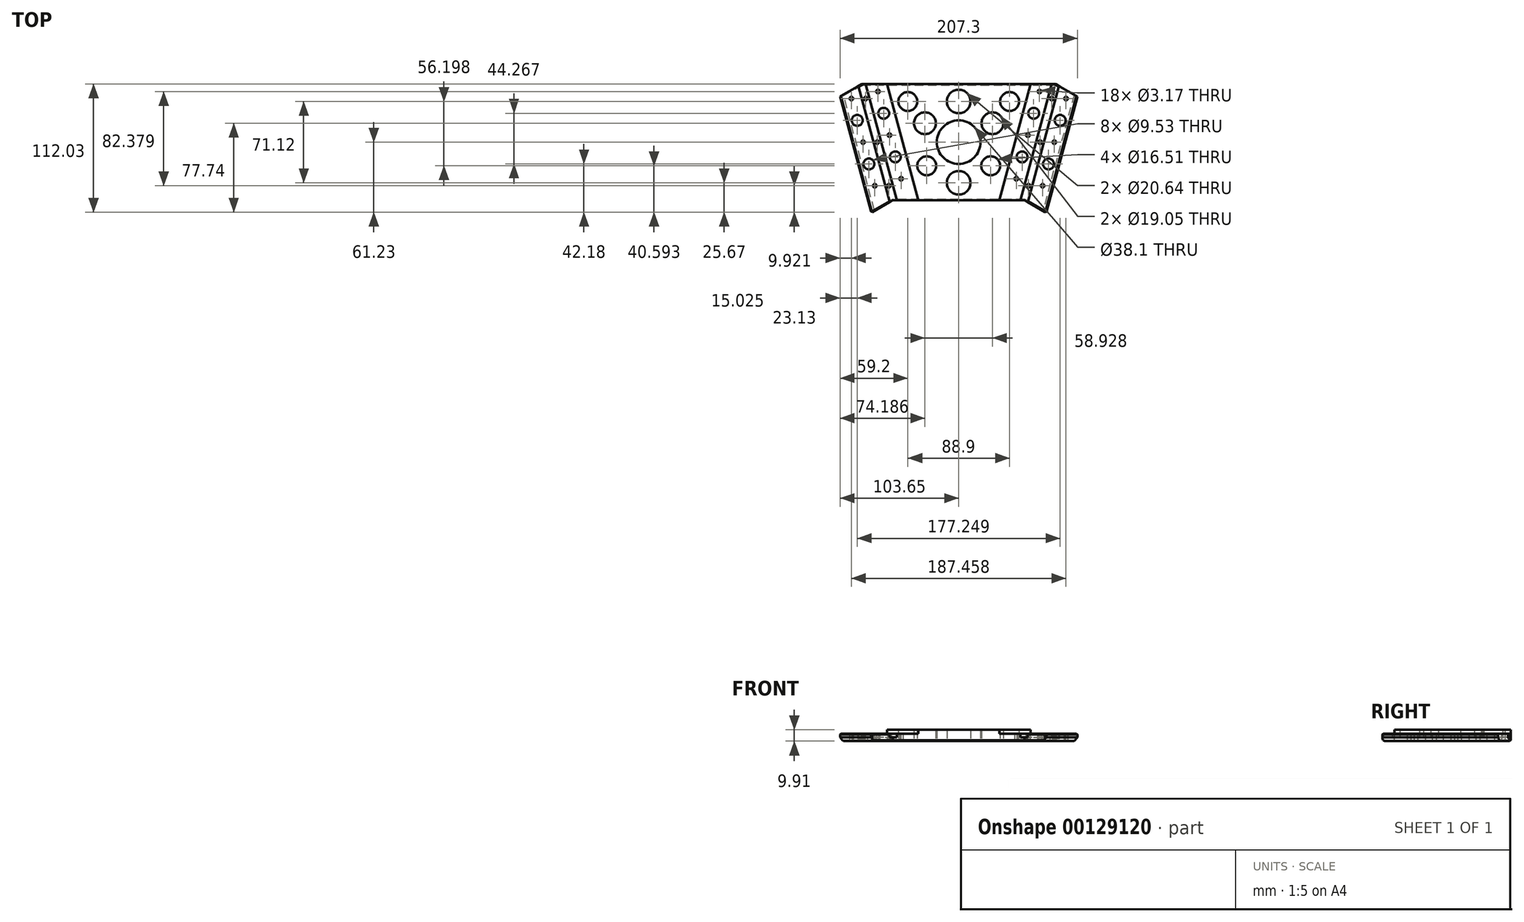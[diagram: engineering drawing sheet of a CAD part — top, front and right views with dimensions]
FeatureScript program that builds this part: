
annotation { "Feature Type Name" : "Feature", "Feature Type Description" : "" }
export const myFeature = defineFeature(function(context is Context, id is Id, definition is map)
    precondition{}
    {
        {
            var Q0;
            Q0=qCreatedBy(makeId("Top.planeOp"),FACE);
            var sketch = newSketch(context, id + "F0", { "sketchPlane" : qUnion([Q0])});
            skLineSegment(sketch, "E0", {"start": v(-79.38, -50.8) * mm, "end": v(0, -50.8) * mm});
            skLineSegment(sketch, "E1", {"start": v(0, -50.8) * mm, "end": v(0, 50.8) * mm});
            skLineSegment(sketch, "E2", {"start": v(0, 50.8) * mm, "end": v(-106.6, 50.8) * mm});
            skLineSegment(sketch, "E3", {"start": v(-106.6, 50.8) * mm, "end": v(-79.38, -50.8) * mm});
            skLineSegment(sketch, "E4.MirrorCS", {"start": v(0, 50.8) * mm, "end": v(106.6, 50.8) * mm});
            skLineSegment(sketch, "E5.MirrorCS", {"start": v(106.6, 50.8) * mm, "end": v(79.38, -50.8) * mm});
            skLineSegment(sketch, "E6.MirrorCS", {"start": v(79.38, -50.8) * mm, "end": v(0, -50.8) * mm});
            skSolve(sketch);
        }
        {
            var Q0;
            Q0=qSketchRegion(id+"F0",true);
            var Q1;
            Q1=qSketchRegion(id+"F2",true);
            extrude(context, id + "F1", {"entities" : qUnion([Q0, Q1]), "depth" : 13.08 * mm});
        }
        {
            var Q0;
            Q0=makeQuery(id+"F1.opExtrude","CAP_FACE",FACE,{"disambiguationData":[OSD([sQuery(id+"F0.wireOp",EDGE,"E0"),sQuery(id+"F0.wireOp",EDGE,"E1"),sQuery(id+"F0.wireOp",EDGE,"E2"),sQuery(id+"F0.wireOp",EDGE,"E3")])],"isStart":false});
            var sketch = newSketch(context, id + "F2", { "sketchPlane" : qUnion([Q0])});
            skLineSegment(sketch, "E7", {"start": v(-87.93, 50.8) * mm, "end": v(-60.7, -50.8) * mm});
            skLineSegment(sketch, "E8", {"start": v(-60.7, -50.8) * mm, "end": v(-54, -50.8) * mm});
            skLineSegment(sketch, "E9", {"start": v(-54, -50.8) * mm, "end": v(-81.22, 50.8) * mm});
            skLineSegment(sketch, "E10", {"start": v(-81.22, 50.8) * mm, "end": v(-87.93, 50.8) * mm});
            skLineSegment(sketch, "E11.MirrorCS", {"start": v(54, -50.8) * mm, "end": v(81.22, 50.8) * mm});
            skLineSegment(sketch, "E12.MirrorCS", {"start": v(60.7, -50.8) * mm, "end": v(54, -50.8) * mm});
            skLineSegment(sketch, "E13.MirrorCS", {"start": v(87.93, 50.8) * mm, "end": v(60.7, -50.8) * mm});
            skLineSegment(sketch, "E14.MirrorCS", {"start": v(81.22, 50.8) * mm, "end": v(87.93, 50.8) * mm});
            skSolve(sketch);
        }
        {
            var Q0;
            Q0=qSketchRegion(id+"F2",true);
            extrude(context, id + "F3", {"entities" : qUnion([Q0]), "operationType" : NewBodyOperationType.REMOVE, "oppositeDirection" : true, "depth" : 9.9 * mm});
        }
        {
            var Q0;
            {var subQ0=sQuery(id+"F0.wireOp",EDGE,"E0");var subQ1=sQuery(id+"F0.wireOp",EDGE,"E2");var subQ2=sQuery(id+"F0.wireOp",EDGE,"E3");Q0=makeQuery(id+"F3.boolean.opBoolean","SPLIT",FACE,{"disambiguationData":[TD([makeQuery(id+"F1.opExtrude","SWEPT_FACE",FACE,{"disambiguationData":[OSD([subQ2])]})])],"derivedFrom":makeQuery(id+"F1.opExtrude","CAP_FACE",FACE,{"disambiguationData":[OSD([subQ0,sQuery(id+"F0.wireOp",EDGE,"E1"),subQ1,subQ2])],"isStart":false})});}
            var sketch = newSketch(context, id + "F4", { "sketchPlane" : qUnion([Q0])});
            skLineSegment(sketch, "E15", {"start": v(-106.6, 50.8) * mm, "end": v(-87.93, 50.8) * mm});
            skLineSegment(sketch, "E16", {"start": v(-87.93, 50.8) * mm, "end": v(-60.7, -50.8) * mm});
            skLineSegment(sketch, "E17", {"start": v(-60.7, -50.8) * mm, "end": v(-79.38, -50.8) * mm});
            skLineSegment(sketch, "E18", {"start": v(-79.37, -50.8) * mm, "end": v(-106.6, 50.8) * mm});
            skLineSegment(sketch, "E19.MirrorCS", {"start": v(87.93, 50.8) * mm, "end": v(60.7, -50.8) * mm});
            skLineSegment(sketch, "E20.MirrorCS", {"start": v(60.7, -50.8) * mm, "end": v(79.38, -50.8) * mm});
            skLineSegment(sketch, "E21.MirrorCS", {"start": v(79.37, -50.8) * mm, "end": v(106.6, 50.8) * mm});
            skLineSegment(sketch, "E22.MirrorCS", {"start": v(106.6, 50.8) * mm, "end": v(87.93, 50.8) * mm});
            skSolve(sketch);
        }
        {
            var Q0;
            Q0=qSketchRegion(id+"F4",true);
            extrude(context, id + "F5", {"entities" : qUnion([Q0]), "operationType" : NewBodyOperationType.REMOVE, "oppositeDirection" : true, "depth" : 6.54 * mm});
        }
        {
            var Q0;
            {var subQ0=sQuery(id+"F0.wireOp",EDGE,"E6.MirrorCS");var subQ1=sQuery(id+"F0.wireOp",EDGE,"E0");var subQ2=sQuery(id+"F0.wireOp",EDGE,"E4.MirrorCS");var subQ3=sQuery(id+"F0.wireOp",EDGE,"E2");Q0=makeQuery(id+"F3.boolean.opBoolean","SPLIT",FACE,{"disambiguationData":[TD([makeQuery(id+"F3.opExtrude","SWEPT_FACE",FACE,{"disambiguationData":[OSD([sQuery(id+"F2.wireOp",EDGE,"E9")])]})])],"derivedFrom":makeQuery(id+"F1.opExtrude","CAP_FACE",FACE,{"disambiguationData":[OSD([subQ1,subQ3,sQuery(id+"F0.wireOp",EDGE,"E3"),subQ2,sQuery(id+"F0.wireOp",EDGE,"E5.MirrorCS"),subQ0])],"isStart":false})});}
            var sketch = newSketch(context, id + "F6", { "sketchPlane" : qUnion([Q0])});
            skLineSegment(sketch, "E23", {"start": v(-81.22, 50.8) * mm, "end": v(81.22, 50.8) * mm});
            skLineSegment(sketch, "E24", {"start": v(81.22, 50.8) * mm, "end": v(54, -50.8) * mm});
            skLineSegment(sketch, "E25", {"start": v(54, -50.8) * mm, "end": v(-54, -50.8) * mm});
            skLineSegment(sketch, "E26", {"start": v(-54, -50.8) * mm, "end": v(-81.22, 50.8) * mm});
            skSolve(sketch);
        }
        {
            var Q0;
            Q0=qSketchRegion(id+"F6",true);
            extrude(context, id + "F7", {"entities" : qUnion([Q0]), "operationType" : NewBodyOperationType.REMOVE, "oppositeDirection" : true, "depth" : 3.17 * mm});
        }
        {
            var Q0;
            Q0=qCreatedBy(makeId("Top.planeOp"),FACE);
            var sketch = newSketch(context, id + "F8", { "sketchPlane" : qUnion([Q0])});
            skCircle(sketch, "E27", {"center": v(-93.73, 38.1) * mm, "radius": 1.59 * mm});
            skCircle(sketch, "E28", {"center": v(-83.52, 0) * mm, "radius": 1.59 * mm});
            skCircle(sketch, "E29", {"center": v(-73.31, -38.1) * mm, "radius": 1.59 * mm});
            skCircle(sketch, "E30", {"center": v(-78.42, -19.05) * mm, "radius": 4.76 * mm});
            skCircle(sketch, "E31", {"center": v(-88.62, 19.05) * mm, "radius": 4.76 * mm});
            skCircle(sketch, "E32", {"center": v(0, 0) * mm, "radius": 19.05 * mm});
            skCircle(sketch, "E33.MirrorC", {"center": v(73.31, -38.1) * mm, "radius": 1.59 * mm});
            skCircle(sketch, "E34.MirrorC", {"center": v(78.42, -19.05) * mm, "radius": 4.76 * mm});
            skCircle(sketch, "E35.MirrorC", {"center": v(83.52, 0) * mm, "radius": 1.59 * mm});
            skCircle(sketch, "E36.MirrorC", {"center": v(88.62, 19.05) * mm, "radius": 4.76 * mm});
            skCircle(sketch, "E37.MirrorC", {"center": v(93.73, 38.1) * mm, "radius": 1.59 * mm});
            skCircle(sketch, "E38", {"center": v(0, -35.56) * mm, "radius": 10.32 * mm});
            skCircle(sketch, "E39", {"center": v(0, 35.56) * mm, "radius": 10.32 * mm});
            skCircle(sketch, "E40", {"center": v(-29.46, 16.51) * mm, "radius": 9.53 * mm});
            skCircle(sketch, "E41", {"center": v(-27.94, -20.64) * mm, "radius": 8.26 * mm});
            skCircle(sketch, "E42.MirrorC", {"center": v(29.46, 16.51) * mm, "radius": 9.53 * mm});
            skCircle(sketch, "E43.MirrorC", {"center": v(27.94, -20.64) * mm, "radius": 8.26 * mm});
            skLineSegment(sketch, "E44", {"start": v(-85.97, 55.55) * mm, "end": v(-55.01, -60.54) * mm});
            skCircle(sketch, "E45", {"center": v(-81.32, 38.1) * mm, "radius": 1.59 * mm});
            skCircle(sketch, "E46", {"center": v(-61, -38.1) * mm, "radius": 1.59 * mm});
            skCircle(sketch, "E47", {"center": v(-71.16, 0) * mm, "radius": 1.59 * mm});
            skCircle(sketch, "E48.MirrorC", {"center": v(-70.56, 44.28) * mm, "radius": 1.59 * mm});
            skCircle(sketch, "E49.MirrorC", {"center": v(-60.44, 6.15) * mm, "radius": 1.59 * mm});
            skCircle(sketch, "E50.MirrorC", {"center": v(-50.32, -31.97) * mm, "radius": 1.59 * mm});
            skCircle(sketch, "E51.MirrorC", {"center": v(70.56, 44.28) * mm, "radius": 1.59 * mm});
            skCircle(sketch, "E52.MirrorC", {"center": v(60.44, 6.15) * mm, "radius": 1.59 * mm});
            skCircle(sketch, "E53.MirrorC", {"center": v(50.32, -31.97) * mm, "radius": 1.59 * mm});
            skCircle(sketch, "E54.MirrorC", {"center": v(61, -38.1) * mm, "radius": 1.59 * mm});
            skCircle(sketch, "E55.MirrorC", {"center": v(71.16, 0) * mm, "radius": 1.59 * mm});
            skCircle(sketch, "E56.MirrorC", {"center": v(81.32, 38.1) * mm, "radius": 1.59 * mm});
            skCircle(sketch, "E57.MirrorC", {"center": v(-55.38, -12.9) * mm, "radius": 4.76 * mm});
            skCircle(sketch, "E58.MirrorC", {"center": v(-65.5, 25.22) * mm, "radius": 4.76 * mm});
            skCircle(sketch, "E59.MirrorC", {"center": v(65.5, 25.22) * mm, "radius": 4.76 * mm});
            skCircle(sketch, "E60.MirrorC", {"center": v(55.38, -12.9) * mm, "radius": 4.76 * mm});
            skCircle(sketch, "E61", {"center": v(-44.45, 35.56) * mm, "radius": 8.26 * mm});
            skCircle(sketch, "E62.MirrorC", {"center": v(44.45, 35.56) * mm, "radius": 8.26 * mm});
            skSolve(sketch);
        }
        {
            var Q0;
            Q0=qSketchRegion(id+"F8",true);
            extrude(context, id + "F9", {"entities" : qUnion([Q0]), "operationType" : NewBodyOperationType.REMOVE, "endBound" : BoundingType.THROUGH_ALL, "depth" : 25.4 * mm});
        }
        {
            var Q0;
            Q0=makeQuery(id+"F5.boolean.opBoolean","COPY",FACE,{"derivedFrom":makeQuery(id+"F5.opExtrude","CAP_FACE",FACE,{"disambiguationData":[OSD([sQuery(id+"F4.wireOp",EDGE,"E15"),sQuery(id+"F4.wireOp",EDGE,"E16"),sQuery(id+"F4.wireOp",EDGE,"E17"),sQuery(id+"F4.wireOp",EDGE,"E18")])],"isStart":false})});
            var sketch = newSketch(context, id + "F10", { "sketchPlane" : qUnion([Q0])});
            skLineSegment(sketch, "E63", {"start": v(-84.59, 50.8) * mm, "end": v(-103.65, 39.8) * mm});
            skLineSegment(sketch, "E64", {"start": v(-84.59, 50.8) * mm, "end": v(-106.6, 50.8) * mm});
            skLineSegment(sketch, "E65", {"start": v(-106.6, 50.8) * mm, "end": v(-103.65, 39.8) * mm});
            skLineSegment(sketch, "E66.MirrorCS", {"start": v(84.59, 50.8) * mm, "end": v(103.65, 39.8) * mm});
            skLineSegment(sketch, "E67.MirrorCS", {"start": v(84.59, 50.8) * mm, "end": v(106.6, 50.8) * mm});
            skLineSegment(sketch, "E68.MirrorCS", {"start": v(106.6, 50.8) * mm, "end": v(103.65, 39.8) * mm});
            skSolve(sketch);
        }
        {
            var Q0;
            Q0=qSketchRegion(id+"F10",true);
            extrude(context, id + "F11", {"entities" : qUnion([Q0]), "operationType" : NewBodyOperationType.REMOVE, "endBound" : BoundingType.THROUGH_ALL, "oppositeDirection" : true, "depth" : 25.4 * mm});
        }
        {
            var Q0;
            Q0=makeQuery(id+"F5.boolean.opBoolean","COPY",FACE,{"derivedFrom":makeQuery(id+"F5.opExtrude","CAP_FACE",FACE,{"disambiguationData":[OSD([sQuery(id+"F4.wireOp",EDGE,"E15"),sQuery(id+"F4.wireOp",EDGE,"E16"),sQuery(id+"F4.wireOp",EDGE,"E17"),sQuery(id+"F4.wireOp",EDGE,"E18")])],"isStart":false})});
            var sketch = newSketch(context, id + "F12", { "sketchPlane" : qUnion([Q0])});
            skLineSegment(sketch, "E69", {"start": v(-79.38, -50.8) * mm, "end": v(-57.48, -50.8) * mm});
            skLineSegment(sketch, "E70", {"start": v(-76.44, -61.75) * mm, "end": v(-79.38, -50.8) * mm});
            skLineSegment(sketch, "E71.MirrorCS", {"start": v(57.48, -50.8) * mm, "end": v(76.44, -61.75) * mm});
            skLineSegment(sketch, "E72.MirrorCS", {"start": v(76.44, -61.75) * mm, "end": v(79.38, -50.8) * mm});
            skLineSegment(sketch, "E73.MirrorCS", {"start": v(79.38, -50.8) * mm, "end": v(57.48, -50.8) * mm});
            skLineSegment(sketch, "E74", {"start": v(-90.42, 72.13) * mm, "end": v(-51.77, -72.1) * mm});
            skLineSegment(sketch, "E75", {"start": v(-76.44, -61.75) * mm, "end": v(-57.48, -50.8) * mm});
            skSolve(sketch);
        }
        {
            var Q0;
            Q0=qSketchRegion(id+"F12",true);
            extrude(context, id + "F13", {"entities" : qUnion([Q0]), "operationType" : NewBodyOperationType.ADD, "oppositeDirection" : true, "depth" : 6.54 * mm});
        }
        {
            var Q0;
            Q0=makeQuery(id+"F13.boolean.opBoolean","MERGE",FACE,{"derivedFrom":[makeQuery(id+"F5.boolean.opBoolean","COPY",FACE,{"derivedFrom":makeQuery(id+"F5.opExtrude","CAP_FACE",FACE,{"disambiguationData":[OSD([sQuery(id+"F4.wireOp",EDGE,"E15"),sQuery(id+"F4.wireOp",EDGE,"E16"),sQuery(id+"F4.wireOp",EDGE,"E17"),sQuery(id+"F4.wireOp",EDGE,"E18")])],"isStart":false})}),makeQuery(id+"F13.opExtrude","CAP_FACE",FACE,{"disambiguationData":[OSD([sQuery(id+"F12.wireOp",EDGE,"cvvx7mj1-Xfs7-jjY3-ojys-tjZEVBZnVbbF"),sQuery(id+"F12.wireOp",EDGE,"E69"),sQuery(id+"F12.wireOp",EDGE,"E70")])],"isStart":true})]});
            var sketch = newSketch(context, id + "F14", { "sketchPlane" : qUnion([Q0])});
            skLineSegment(sketch, "E76", {"start": v(-60.7, -50.8) * mm, "end": v(-60.27, -52.41) * mm});
            skLineSegment(sketch, "E77", {"start": v(-60.27, -52.41) * mm, "end": v(-57.48, -50.8) * mm});
            skLineSegment(sketch, "E78", {"start": v(-57.48, -50.8) * mm, "end": v(-60.7, -50.8) * mm});
            skLineSegment(sketch, "E79.MirrorCS", {"start": v(60.27, -52.41) * mm, "end": v(57.48, -50.8) * mm});
            skLineSegment(sketch, "E80.MirrorCS", {"start": v(57.48, -50.8) * mm, "end": v(60.7, -50.8) * mm});
            skLineSegment(sketch, "E81.MirrorCS", {"start": v(60.7, -50.8) * mm, "end": v(60.27, -52.41) * mm});
            skSolve(sketch);
        }
        {
            var Q0;
            Q0=qSketchRegion(id+"F14",true);
            extrude(context, id + "F15", {"entities" : qUnion([Q0]), "operationType" : NewBodyOperationType.REMOVE, "oppositeDirection" : true, "depth" : 3.37 * mm});
        }
        {
            var Q0;
            Q0=makeQuery(id+"F7.boolean.opBoolean","COPY",FACE,{"derivedFrom":makeQuery(id+"F7.opExtrude","CAP_FACE",FACE,{"disambiguationData":[OSD([sQuery(id+"F6.wireOp",EDGE,"E23"),sQuery(id+"F6.wireOp",EDGE,"E24"),sQuery(id+"F6.wireOp",EDGE,"E25"),sQuery(id+"F6.wireOp",EDGE,"E26")])],"isStart":false})});
            var sketch = newSketch(context, id + "F16", { "sketchPlane" : qUnion([Q0])});
            skLineSegment(sketch, "E82", {"start": v(-81.22, 50.8) * mm, "end": v(-54, -50.8) * mm});
            skLineSegment(sketch, "E83", {"start": v(-54, -50.8) * mm, "end": v(-35.44, -50.8) * mm});
            skLineSegment(sketch, "E84", {"start": v(-35.44, -50.8) * mm, "end": v(-62.66, 50.8) * mm});
            skLineSegment(sketch, "E85", {"start": v(-62.66, 50.8) * mm, "end": v(-81.22, 50.8) * mm});
            skLineSegment(sketch, "E86.MirrorCS", {"start": v(35.44, -50.8) * mm, "end": v(62.66, 50.8) * mm});
            skLineSegment(sketch, "E87.MirrorCS", {"start": v(62.66, 50.8) * mm, "end": v(81.22, 50.8) * mm});
            skLineSegment(sketch, "E88.MirrorCS", {"start": v(81.22, 50.8) * mm, "end": v(54, -50.8) * mm});
            skLineSegment(sketch, "E89.MirrorCS", {"start": v(54, -50.8) * mm, "end": v(35.44, -50.8) * mm});
            skSolve(sketch);
        }
        {
            var Q0;
            Q0=qSketchRegion(id+"F16",true);
            extrude(context, id + "F17", {"entities" : qUnion([Q0]), "operationType" : NewBodyOperationType.REMOVE, "oppositeDirection" : true, "depth" : 3.37 * mm});
        }
        {
            var Q0;
            Q0=makeQuery(id+"F13.opExtrude","CAP_EDGE",EDGE,{"disambiguationData":[OSD([sQuery(id+"F12.wireOp",EDGE,"cvvx7mj1-Xfs7-jjY3-ojys-tjZEVBZnVbbF")])],"isStart":false});
            var Q1;
            Q1=makeQuery(id+"F1.opExtrude","CAP_EDGE",EDGE,{"disambiguationData":[OSD([sQuery(id+"F0.wireOp",EDGE,"E0"),sQuery(id+"F0.wireOp",EDGE,"E6.MirrorCS")])],"isStart":true});
            var Q2;
            Q2=makeQuery(id+"F13.opExtrude","CAP_EDGE",EDGE,{"disambiguationData":[OSD([sQuery(id+"F12.wireOp",EDGE,"E71.MirrorCS")])],"isStart":false});
            var Q3;
            Q3=makeQuery(id+"F1.opExtrude","CAP_EDGE",EDGE,{"disambiguationData":[OSD([sQuery(id+"F0.wireOp",EDGE,"E2"),sQuery(id+"F0.wireOp",EDGE,"E4.MirrorCS")])],"isStart":true});
            var Q4;
            Q4=makeQuery(id+"F11.boolean.opBoolean","INTERSECT",EDGE,{"derivedFrom":[makeQuery(id+"F1.opExtrude","CAP_FACE",FACE,{"disambiguationData":[OSD([sQuery(id+"F0.wireOp",EDGE,"E0"),sQuery(id+"F0.wireOp",EDGE,"E2"),sQuery(id+"F0.wireOp",EDGE,"E3"),sQuery(id+"F0.wireOp",EDGE,"E4.MirrorCS"),sQuery(id+"F0.wireOp",EDGE,"E5.MirrorCS"),sQuery(id+"F0.wireOp",EDGE,"E6.MirrorCS")])],"isStart":true}),makeQuery(id+"F11.opExtrude","SWEPT_FACE",FACE,{"disambiguationData":[OSD([sQuery(id+"F10.wireOp",EDGE,"E63")])]})]});
            var Q5;
            Q5=makeQuery(id+"F9.boolean.opBoolean","COPY",EDGE,{"derivedFrom":makeQuery(id+"F9.opExtrude","CAP_EDGE",EDGE,{"disambiguationData":[OSD([sQuery(id+"F8.wireOp",EDGE,"E30")])],"isStart":true})});
            var Q6;
            Q6=makeQuery(id+"F9.boolean.opBoolean","COPY",EDGE,{"derivedFrom":makeQuery(id+"F9.opExtrude","CAP_EDGE",EDGE,{"disambiguationData":[OSD([sQuery(id+"F8.wireOp",EDGE,"E31")])],"isStart":true})});
            var Q7;
            Q7=makeQuery(id+"F9.boolean.opBoolean","COPY",EDGE,{"derivedFrom":makeQuery(id+"F9.opExtrude","CAP_EDGE",EDGE,{"disambiguationData":[OSD([sQuery(id+"F8.wireOp",EDGE,"E27")])],"isStart":true})});
            var Q8;
            Q8=makeQuery(id+"F9.boolean.opBoolean","COPY",EDGE,{"derivedFrom":makeQuery(id+"F9.opExtrude","CAP_EDGE",EDGE,{"disambiguationData":[OSD([sQuery(id+"F8.wireOp",EDGE,"E45")])],"isStart":true})});
            var Q9;
            Q9=makeQuery(id+"F9.boolean.opBoolean","COPY",EDGE,{"derivedFrom":makeQuery(id+"F9.opExtrude","CAP_EDGE",EDGE,{"disambiguationData":[OSD([sQuery(id+"F8.wireOp",EDGE,"E48.MirrorC")])],"isStart":true})});
            var Q10;
            Q10=makeQuery(id+"F9.boolean.opBoolean","COPY",EDGE,{"derivedFrom":makeQuery(id+"F9.opExtrude","CAP_EDGE",EDGE,{"disambiguationData":[OSD([sQuery(id+"F8.wireOp",EDGE,"E58.MirrorC")])],"isStart":true})});
            var Q11;
            Q11=makeQuery(id+"F9.boolean.opBoolean","COPY",EDGE,{"derivedFrom":makeQuery(id+"F9.opExtrude","CAP_EDGE",EDGE,{"disambiguationData":[OSD([sQuery(id+"F8.wireOp",EDGE,"E49.MirrorC")])],"isStart":true})});
            var Q12;
            Q12=makeQuery(id+"F9.boolean.opBoolean","COPY",EDGE,{"derivedFrom":makeQuery(id+"F9.opExtrude","CAP_EDGE",EDGE,{"disambiguationData":[OSD([sQuery(id+"F8.wireOp",EDGE,"E47")])],"isStart":true})});
            var Q13;
            Q13=makeQuery(id+"F9.boolean.opBoolean","COPY",EDGE,{"derivedFrom":makeQuery(id+"F9.opExtrude","CAP_EDGE",EDGE,{"disambiguationData":[OSD([sQuery(id+"F8.wireOp",EDGE,"E28")])],"isStart":true})});
            var Q14;
            Q14=makeQuery(id+"F9.boolean.opBoolean","COPY",EDGE,{"derivedFrom":makeQuery(id+"F9.opExtrude","CAP_EDGE",EDGE,{"disambiguationData":[OSD([sQuery(id+"F8.wireOp",EDGE,"E29")])],"isStart":true})});
            var Q15;
            Q15=makeQuery(id+"F9.boolean.opBoolean","COPY",EDGE,{"derivedFrom":makeQuery(id+"F9.opExtrude","CAP_EDGE",EDGE,{"disambiguationData":[OSD([sQuery(id+"F8.wireOp",EDGE,"E46")])],"isStart":true})});
            var Q16;
            Q16=makeQuery(id+"F9.boolean.opBoolean","COPY",EDGE,{"derivedFrom":makeQuery(id+"F9.opExtrude","CAP_EDGE",EDGE,{"disambiguationData":[OSD([sQuery(id+"F8.wireOp",EDGE,"E50.MirrorC")])],"isStart":true})});
            var Q17;
            Q17=makeQuery(id+"F9.boolean.opBoolean","COPY",EDGE,{"derivedFrom":makeQuery(id+"F9.opExtrude","CAP_EDGE",EDGE,{"disambiguationData":[OSD([sQuery(id+"F8.wireOp",EDGE,"E57.MirrorC")])],"isStart":true})});
            var Q18;
            Q18=makeQuery(id+"F9.boolean.opBoolean","COPY",EDGE,{"derivedFrom":makeQuery(id+"F9.opExtrude","CAP_EDGE",EDGE,{"disambiguationData":[OSD([sQuery(id+"F8.wireOp",EDGE,"3OGpdaGj-J4Qy-kOOw-tfdq-MqeFCowQVxvU")])],"isStart":true})});
            var Q19;
            Q19=makeQuery(id+"F9.boolean.opBoolean","COPY",EDGE,{"derivedFrom":makeQuery(id+"F9.opExtrude","CAP_EDGE",EDGE,{"disambiguationData":[OSD([sQuery(id+"F8.wireOp",EDGE,"fb806Q8q-M2gs-CntQ-5ERf-59aPclVVQ7Sl")])],"isStart":true})});
            var Q20;
            Q20=makeQuery(id+"F9.boolean.opBoolean","COPY",EDGE,{"derivedFrom":makeQuery(id+"F9.opExtrude","CAP_EDGE",EDGE,{"disambiguationData":[OSD([sQuery(id+"F8.wireOp",EDGE,"K7RIXJCq-95tg-0nTO-jRqB-ZHNu7gw8pOAv.top")])],"isStart":true})});
            var Q21;
            Q21=makeQuery(id+"F9.boolean.opBoolean","COPY",EDGE,{"derivedFrom":makeQuery(id+"F9.opExtrude","CAP_EDGE",EDGE,{"disambiguationData":[OSD([sQuery(id+"F8.wireOp",EDGE,"E40")])],"isStart":true})});
            var Q22;
            Q22=makeQuery(id+"F9.boolean.opBoolean","COPY",EDGE,{"derivedFrom":makeQuery(id+"F9.opExtrude","CAP_EDGE",EDGE,{"disambiguationData":[OSD([sQuery(id+"F8.wireOp",EDGE,"E41")])],"isStart":true})});
            var Q23;
            Q23=makeQuery(id+"F9.boolean.opBoolean","COPY",EDGE,{"derivedFrom":makeQuery(id+"F9.opExtrude","CAP_EDGE",EDGE,{"disambiguationData":[OSD([sQuery(id+"F8.wireOp",EDGE,"sYgtS7vl-is4R-K6Nf-HOrt-AmKfPqeVfDI7.top")])],"isStart":true})});
            var Q24;
            Q24=makeQuery(id+"F9.boolean.opBoolean","COPY",EDGE,{"derivedFrom":makeQuery(id+"F9.opExtrude","CAP_EDGE",EDGE,{"disambiguationData":[OSD([sQuery(id+"F8.wireOp",EDGE,"a1322306-f819-4c98-93d9-016f1574bdc60.MirrorCS")])],"isStart":true})});
            var Q25;
            Q25=makeQuery(id+"F9.boolean.opBoolean","COPY",EDGE,{"derivedFrom":makeQuery(id+"F9.opExtrude","CAP_EDGE",EDGE,{"disambiguationData":[OSD([sQuery(id+"F8.wireOp",EDGE,"E33.MirrorC")])],"isStart":true})});
            var Q26;
            Q26=makeQuery(id+"F9.boolean.opBoolean","COPY",EDGE,{"derivedFrom":makeQuery(id+"F9.opExtrude","CAP_EDGE",EDGE,{"disambiguationData":[OSD([sQuery(id+"F8.wireOp",EDGE,"E54.MirrorC")])],"isStart":true})});
            var Q27;
            Q27=makeQuery(id+"F9.boolean.opBoolean","COPY",EDGE,{"derivedFrom":makeQuery(id+"F9.opExtrude","CAP_EDGE",EDGE,{"disambiguationData":[OSD([sQuery(id+"F8.wireOp",EDGE,"E53.MirrorC")])],"isStart":true})});
            var Q28;
            Q28=makeQuery(id+"F9.boolean.opBoolean","COPY",EDGE,{"derivedFrom":makeQuery(id+"F9.opExtrude","CAP_EDGE",EDGE,{"disambiguationData":[OSD([sQuery(id+"F8.wireOp",EDGE,"E52.MirrorC")])],"isStart":true})});
            var Q29;
            Q29=makeQuery(id+"F9.boolean.opBoolean","COPY",EDGE,{"derivedFrom":makeQuery(id+"F9.opExtrude","CAP_EDGE",EDGE,{"disambiguationData":[OSD([sQuery(id+"F8.wireOp",EDGE,"E55.MirrorC")])],"isStart":true})});
            var Q30;
            Q30=makeQuery(id+"F9.boolean.opBoolean","COPY",EDGE,{"derivedFrom":makeQuery(id+"F9.opExtrude","CAP_EDGE",EDGE,{"disambiguationData":[OSD([sQuery(id+"F8.wireOp",EDGE,"E35.MirrorC")])],"isStart":true})});
            var Q31;
            Q31=makeQuery(id+"F9.boolean.opBoolean","COPY",EDGE,{"derivedFrom":makeQuery(id+"F9.opExtrude","CAP_EDGE",EDGE,{"disambiguationData":[OSD([sQuery(id+"F8.wireOp",EDGE,"E36.MirrorC")])],"isStart":true})});
            var Q32;
            Q32=makeQuery(id+"F9.boolean.opBoolean","COPY",EDGE,{"derivedFrom":makeQuery(id+"F9.opExtrude","CAP_EDGE",EDGE,{"disambiguationData":[OSD([sQuery(id+"F8.wireOp",EDGE,"E37.MirrorC")])],"isStart":true})});
            var Q33;
            Q33=makeQuery(id+"F9.boolean.opBoolean","COPY",EDGE,{"derivedFrom":makeQuery(id+"F9.opExtrude","CAP_EDGE",EDGE,{"disambiguationData":[OSD([sQuery(id+"F8.wireOp",EDGE,"E56.MirrorC")])],"isStart":true})});
            var Q34;
            Q34=makeQuery(id+"F9.boolean.opBoolean","COPY",EDGE,{"derivedFrom":makeQuery(id+"F9.opExtrude","CAP_EDGE",EDGE,{"disambiguationData":[OSD([sQuery(id+"F8.wireOp",EDGE,"E51.MirrorC")])],"isStart":true})});
            var Q35;
            Q35=makeQuery(id+"F9.boolean.opBoolean","COPY",EDGE,{"derivedFrom":makeQuery(id+"F9.opExtrude","CAP_EDGE",EDGE,{"disambiguationData":[OSD([sQuery(id+"F8.wireOp",EDGE,"E60.MirrorC")])],"isStart":true})});
            var Q36;
            Q36=makeQuery(id+"F9.boolean.opBoolean","COPY",EDGE,{"derivedFrom":makeQuery(id+"F9.opExtrude","CAP_EDGE",EDGE,{"disambiguationData":[OSD([sQuery(id+"F8.wireOp",EDGE,"E34.MirrorC")])],"isStart":true})});
            var Q37;
            Q37=makeQuery(id+"F9.boolean.opBoolean","COPY",EDGE,{"derivedFrom":makeQuery(id+"F9.opExtrude","CAP_EDGE",EDGE,{"disambiguationData":[OSD([sQuery(id+"F8.wireOp",EDGE,"E59.MirrorC")])],"isStart":true})});
            var Q38;
            Q38=makeQuery(id+"F9.boolean.opBoolean","COPY",EDGE,{"derivedFrom":makeQuery(id+"F9.opExtrude","CAP_EDGE",EDGE,{"disambiguationData":[OSD([sQuery(id+"F8.wireOp",EDGE,"b654174b-73a5-441f-8088-a68699b314700.MirrorC")])],"isStart":true})});
            var Q39;
            Q39=makeQuery(id+"F9.boolean.opBoolean","COPY",EDGE,{"derivedFrom":makeQuery(id+"F9.opExtrude","CAP_EDGE",EDGE,{"disambiguationData":[OSD([sQuery(id+"F8.wireOp",EDGE,"b5091e9b-011f-4b6e-8bab-6b4f0b875eb90.MirrorCS")])],"isStart":true})});
            var Q40;
            Q40=makeQuery(id+"F9.boolean.opBoolean","COPY",EDGE,{"derivedFrom":makeQuery(id+"F9.opExtrude","CAP_EDGE",EDGE,{"disambiguationData":[OSD([sQuery(id+"F8.wireOp",EDGE,"E42.MirrorC")])],"isStart":true})});
            var Q41;
            Q41=makeQuery(id+"F9.boolean.opBoolean","COPY",EDGE,{"derivedFrom":makeQuery(id+"F9.opExtrude","CAP_EDGE",EDGE,{"disambiguationData":[OSD([sQuery(id+"F8.wireOp",EDGE,"E39")])],"isStart":true})});
            var Q42;
            Q42=makeQuery(id+"F9.boolean.opBoolean","COPY",EDGE,{"derivedFrom":makeQuery(id+"F9.opExtrude","CAP_EDGE",EDGE,{"disambiguationData":[OSD([sQuery(id+"F8.wireOp",EDGE,"E32")])],"isStart":true})});
            var Q43;
            Q43=makeQuery(id+"F9.boolean.opBoolean","COPY",EDGE,{"derivedFrom":makeQuery(id+"F9.opExtrude","CAP_EDGE",EDGE,{"disambiguationData":[OSD([sQuery(id+"F8.wireOp",EDGE,"E43.MirrorC")])],"isStart":true})});
            var Q44;
            Q44=makeQuery(id+"F9.boolean.opBoolean","COPY",EDGE,{"derivedFrom":makeQuery(id+"F9.opExtrude","CAP_EDGE",EDGE,{"disambiguationData":[OSD([sQuery(id+"F8.wireOp",EDGE,"bedb36fd-e39d-498e-9229-9454b53f9d520.MirrorC")])],"isStart":true})});
            var Q45;
            Q45=makeQuery(id+"F9.boolean.opBoolean","COPY",EDGE,{"derivedFrom":makeQuery(id+"F9.opExtrude","CAP_EDGE",EDGE,{"disambiguationData":[OSD([sQuery(id+"F8.wireOp",EDGE,"E38")])],"isStart":true})});
            var Q46;
            Q46=makeQuery(id+"F17.boolean.opBoolean","COPY",EDGE,{"disambiguationData":[OD(4.0)],"derivedFrom":makeQuery(id+"F17.opExtrude","CAP_EDGE",EDGE,{"disambiguationData":[OSD([sQuery(id+"F16.wireOp",EDGE,"E84")])],"isStart":true})});
            var Q47;
            Q47=makeQuery(id+"F17.boolean.opBoolean","COPY",EDGE,{"disambiguationData":[OD(2.0)],"derivedFrom":makeQuery(id+"F17.opExtrude","CAP_EDGE",EDGE,{"disambiguationData":[OSD([sQuery(id+"F16.wireOp",EDGE,"E84")])],"isStart":true})});
            var Q48;
            Q48=makeQuery(id+"F17.boolean.opBoolean","COPY",EDGE,{"disambiguationData":[OD(0.0)],"derivedFrom":makeQuery(id+"F17.opExtrude","CAP_EDGE",EDGE,{"disambiguationData":[OSD([sQuery(id+"F16.wireOp",EDGE,"E84")])],"isStart":true})});
            var Q49;
            Q49=makeQuery(id+"F17.boolean.opBoolean","COPY",EDGE,{"disambiguationData":[OD(1.0)],"derivedFrom":makeQuery(id+"F17.opExtrude","CAP_EDGE",EDGE,{"disambiguationData":[OSD([sQuery(id+"F16.wireOp",EDGE,"E84")])],"isStart":true})});
            var Q50;
            Q50=makeQuery(id+"F17.boolean.opBoolean","COPY",EDGE,{"disambiguationData":[OD(3.0)],"derivedFrom":makeQuery(id+"F17.opExtrude","CAP_EDGE",EDGE,{"disambiguationData":[OSD([sQuery(id+"F16.wireOp",EDGE,"E84")])],"isStart":true})});
            var Q51;
            Q51=makeQuery(id+"F17.boolean.opBoolean","COPY",EDGE,{"disambiguationData":[OD(0.0)],"derivedFrom":makeQuery(id+"F17.opExtrude","CAP_EDGE",EDGE,{"disambiguationData":[OSD([sQuery(id+"F16.wireOp",EDGE,"E86.MirrorCS")])],"isStart":true})});
            var Q52;
            Q52=makeQuery(id+"F17.boolean.opBoolean","COPY",EDGE,{"disambiguationData":[OD(3.0)],"derivedFrom":makeQuery(id+"F17.opExtrude","CAP_EDGE",EDGE,{"disambiguationData":[OSD([sQuery(id+"F16.wireOp",EDGE,"E86.MirrorCS")])],"isStart":true})});
            var Q53;
            Q53=makeQuery(id+"F17.boolean.opBoolean","COPY",EDGE,{"disambiguationData":[OD(4.0)],"derivedFrom":makeQuery(id+"F17.opExtrude","CAP_EDGE",EDGE,{"disambiguationData":[OSD([sQuery(id+"F16.wireOp",EDGE,"E86.MirrorCS")])],"isStart":true})});
            var Q54;
            Q54=makeQuery(id+"F17.boolean.opBoolean","COPY",EDGE,{"disambiguationData":[OD(2.0)],"derivedFrom":makeQuery(id+"F17.opExtrude","CAP_EDGE",EDGE,{"disambiguationData":[OSD([sQuery(id+"F16.wireOp",EDGE,"E86.MirrorCS")])],"isStart":true})});
            var Q55;
            Q55=makeQuery(id+"F17.boolean.opBoolean","COPY",EDGE,{"disambiguationData":[OD(1.0)],"derivedFrom":makeQuery(id+"F17.opExtrude","CAP_EDGE",EDGE,{"disambiguationData":[OSD([sQuery(id+"F16.wireOp",EDGE,"E86.MirrorCS")])],"isStart":true})});
            var Q56;
            Q56=makeQuery(id+"F13.opExtrude","CAP_EDGE",EDGE,{"disambiguationData":[OSD([sQuery(id+"F12.wireOp",EDGE,"E75")])],"isStart":false});
            var Q57;
            Q57=makeQuery(id+"F17.boolean.opBoolean","COPY",EDGE,{"derivedFrom":makeQuery(id+"F17.opExtrude","CAP_EDGE",EDGE,{"disambiguationData":[OSD([sQuery(id+"F16.wireOp",EDGE,"E88.MirrorCS")])],"isStart":false})});
            var Q58;
            Q58=makeQuery(id+"F15.boolean.opBoolean","MERGE",EDGE,{"derivedFrom":[makeQuery(id+"F5.boolean.opBoolean","COPY",EDGE,{"derivedFrom":makeQuery(id+"F5.opExtrude","CAP_EDGE",EDGE,{"disambiguationData":[OSD([sQuery(id+"F4.wireOp",EDGE,"E19.MirrorCS")])],"isStart":false})}),makeQuery(id+"F15.opExtrude","CAP_EDGE",EDGE,{"disambiguationData":[OSD([sQuery(id+"F14.wireOp",EDGE,"E81.MirrorCS")])],"isStart":true})]});
            var Q59;
            Q59=makeQuery(id+"F17.boolean.opBoolean","COPY",EDGE,{"derivedFrom":makeQuery(id+"F17.opExtrude","CAP_EDGE",EDGE,{"disambiguationData":[OSD([sQuery(id+"F16.wireOp",EDGE,"E82")])],"isStart":false})});
            var Q60;
            Q60=makeQuery(id+"F15.boolean.opBoolean","MERGE",EDGE,{"derivedFrom":[makeQuery(id+"F5.boolean.opBoolean","COPY",EDGE,{"derivedFrom":makeQuery(id+"F5.opExtrude","CAP_EDGE",EDGE,{"disambiguationData":[OSD([sQuery(id+"F4.wireOp",EDGE,"E16")])],"isStart":false})}),makeQuery(id+"F15.opExtrude","CAP_EDGE",EDGE,{"disambiguationData":[OSD([sQuery(id+"F14.wireOp",EDGE,"E76")])],"isStart":true})]});
            var Q61;
            Q61=makeQuery(id+"F15.boolean.opBoolean","COPY",EDGE,{"derivedFrom":makeQuery(id+"F15.opExtrude","SWEPT_EDGE",EDGE,{"disambiguationData":[OSD([sQuery(id+"F12.wireOp",EDGE,"E75"),sQuery(id+"F14.wireOp",EDGE,"E76"),sQuery(id+"F14.wireOp",EDGE,"E77")])]})});
            var Q62;
            Q62=makeQuery(id+"F3.boolean.opBoolean","COPY",EDGE,{"derivedFrom":makeQuery(id+"F3.opExtrude","SWEPT_EDGE",EDGE,{"disambiguationData":[OSD([sQuery(id+"F0.wireOp",EDGE,"E0"),sQuery(id+"F0.wireOp",EDGE,"E6.MirrorCS"),sQuery(id+"F2.wireOp",EDGE,"E8"),sQuery(id+"F2.wireOp",EDGE,"E9")])]})});
            var Q63;
            Q63=makeQuery(id+"F17.boolean.opBoolean","COPY",EDGE,{"derivedFrom":makeQuery(id+"F17.opExtrude","SWEPT_EDGE",EDGE,{"disambiguationData":[OSD([sQuery(id+"F6.wireOp",EDGE,"E25"),sQuery(id+"F16.wireOp",EDGE,"E83"),sQuery(id+"F16.wireOp",EDGE,"E84")])]})});
            var Q64;
            Q64=makeQuery(id+"F15.boolean.opBoolean","COPY",EDGE,{"derivedFrom":makeQuery(id+"F15.opExtrude","SWEPT_EDGE",EDGE,{"disambiguationData":[OSD([sQuery(id+"F14.wireOp",EDGE,"E79.MirrorCS"),sQuery(id+"F14.wireOp",EDGE,"E81.MirrorCS")])]})});
            var Q65;
            Q65=makeQuery(id+"F3.boolean.opBoolean","COPY",EDGE,{"derivedFrom":makeQuery(id+"F3.opExtrude","SWEPT_EDGE",EDGE,{"disambiguationData":[OSD([sQuery(id+"F0.wireOp",EDGE,"E0"),sQuery(id+"F0.wireOp",EDGE,"E6.MirrorCS"),sQuery(id+"F2.wireOp",EDGE,"E11.MirrorCS"),sQuery(id+"F2.wireOp",EDGE,"E12.MirrorCS")])]})});
            var Q66;
            Q66=makeQuery(id+"F17.boolean.opBoolean","COPY",EDGE,{"derivedFrom":makeQuery(id+"F17.opExtrude","SWEPT_EDGE",EDGE,{"disambiguationData":[OSD([sQuery(id+"F6.wireOp",EDGE,"E25"),sQuery(id+"F16.wireOp",EDGE,"E86.MirrorCS"),sQuery(id+"F16.wireOp",EDGE,"E89.MirrorCS")])]})});
            var Q67;
            Q67=makeQuery(id+"F11.boolean.opBoolean","INTERSECT",EDGE,{"derivedFrom":[makeQuery(id+"F3.boolean.opBoolean","COPY",FACE,{"derivedFrom":makeQuery(id+"F3.opExtrude","SWEPT_FACE",FACE,{"disambiguationData":[OSD([sQuery(id+"F2.wireOp",EDGE,"E13.MirrorCS")])]})}),makeQuery(id+"F11.opExtrude","SWEPT_FACE",FACE,{"disambiguationData":[OSD([sQuery(id+"F10.wireOp",EDGE,"E66.MirrorCS")])]})]});
            var Q68;
            Q68=makeQuery(id+"F3.boolean.opBoolean","COPY",EDGE,{"derivedFrom":makeQuery(id+"F3.opExtrude","SWEPT_EDGE",EDGE,{"disambiguationData":[OSD([sQuery(id+"F0.wireOp",EDGE,"E2"),sQuery(id+"F0.wireOp",EDGE,"E4.MirrorCS"),sQuery(id+"F2.wireOp",EDGE,"E11.MirrorCS"),sQuery(id+"F2.wireOp",EDGE,"E14.MirrorCS")])]})});
            var Q69;
            Q69=makeQuery(id+"F17.boolean.opBoolean","COPY",EDGE,{"derivedFrom":makeQuery(id+"F17.opExtrude","SWEPT_EDGE",EDGE,{"disambiguationData":[OSD([sQuery(id+"F6.wireOp",EDGE,"E23"),sQuery(id+"F16.wireOp",EDGE,"E86.MirrorCS"),sQuery(id+"F16.wireOp",EDGE,"E87.MirrorCS")])]})});
            var Q70;
            Q70=makeQuery(id+"F17.boolean.opBoolean","COPY",EDGE,{"derivedFrom":makeQuery(id+"F17.opExtrude","SWEPT_EDGE",EDGE,{"disambiguationData":[OSD([sQuery(id+"F6.wireOp",EDGE,"E23"),sQuery(id+"F16.wireOp",EDGE,"E84"),sQuery(id+"F16.wireOp",EDGE,"E85")])]})});
            var Q71;
            Q71=makeQuery(id+"F3.boolean.opBoolean","COPY",EDGE,{"derivedFrom":makeQuery(id+"F3.opExtrude","SWEPT_EDGE",EDGE,{"disambiguationData":[OSD([sQuery(id+"F0.wireOp",EDGE,"E2"),sQuery(id+"F0.wireOp",EDGE,"E4.MirrorCS"),sQuery(id+"F2.wireOp",EDGE,"E9"),sQuery(id+"F2.wireOp",EDGE,"E10")])]})});
            var Q72;
            Q72=makeQuery(id+"F11.boolean.opBoolean","INTERSECT",EDGE,{"derivedFrom":[makeQuery(id+"F3.boolean.opBoolean","COPY",FACE,{"derivedFrom":makeQuery(id+"F3.opExtrude","SWEPT_FACE",FACE,{"disambiguationData":[OSD([sQuery(id+"F2.wireOp",EDGE,"E7")])]})}),makeQuery(id+"F11.opExtrude","SWEPT_FACE",FACE,{"disambiguationData":[OSD([sQuery(id+"F10.wireOp",EDGE,"E63")])]})]});
            var Q73;
            Q73=makeQuery(id+"F13.opExtrude","SWEPT_EDGE",EDGE,{"disambiguationData":[OSD([sQuery(id+"F12.wireOp",EDGE,"E70"),sQuery(id+"F12.wireOp",EDGE,"E75")])]});
            var Q74;
            Q74=makeQuery(id+"F13.opExtrude","SWEPT_EDGE",EDGE,{"disambiguationData":[OSD([sQuery(id+"F12.wireOp",EDGE,"E71.MirrorCS"),sQuery(id+"F12.wireOp",EDGE,"E72.MirrorCS")])]});
            var Q75;
            Q75=makeQuery(id+"F13.opExtrude","CAP_EDGE",EDGE,{"disambiguationData":[OSD([sQuery(id+"F12.wireOp",EDGE,"E71.MirrorCS")])],"isStart":true});
            var Q76;
            Q76=makeQuery(id+"F17.boolean.opBoolean","COPY",EDGE,{"derivedFrom":makeQuery(id+"F17.opExtrude","CAP_EDGE",EDGE,{"disambiguationData":[OSD([sQuery(id+"F16.wireOp",EDGE,"E89.MirrorCS")])],"isStart":false})});
            var Q77;
            Q77=makeQuery(id+"F17.boolean.opBoolean","COPY",EDGE,{"derivedFrom":makeQuery(id+"F17.opExtrude","CAP_EDGE",EDGE,{"disambiguationData":[OSD([sQuery(id+"F16.wireOp",EDGE,"E83")])],"isStart":false})});
            var Q78;
            Q78=makeQuery(id+"F13.opExtrude","CAP_EDGE",EDGE,{"disambiguationData":[OSD([sQuery(id+"F12.wireOp",EDGE,"E75")])],"isStart":true});
            var Q79;
            Q79=makeQuery(id+"F11.boolean.opBoolean","COPY",EDGE,{"derivedFrom":makeQuery(id+"F11.opExtrude","CAP_EDGE",EDGE,{"disambiguationData":[OSD([sQuery(id+"F10.wireOp",EDGE,"E63")])],"isStart":true})});
            var Q80;
            Q80=makeQuery(id+"F17.boolean.opBoolean","COPY",EDGE,{"derivedFrom":makeQuery(id+"F17.opExtrude","CAP_EDGE",EDGE,{"disambiguationData":[OSD([sQuery(id+"F16.wireOp",EDGE,"E85")])],"isStart":false})});
            var Q81;
            Q81=makeQuery(id+"F17.boolean.opBoolean","COPY",EDGE,{"derivedFrom":makeQuery(id+"F17.opExtrude","CAP_EDGE",EDGE,{"disambiguationData":[OSD([sQuery(id+"F16.wireOp",EDGE,"E87.MirrorCS")])],"isStart":false})});
            var Q82;
            Q82=makeQuery(id+"F11.boolean.opBoolean","COPY",EDGE,{"derivedFrom":makeQuery(id+"F11.opExtrude","CAP_EDGE",EDGE,{"disambiguationData":[OSD([sQuery(id+"F10.wireOp",EDGE,"E66.MirrorCS")])],"isStart":true})});
            var Q83;
            {var subQ0=sQuery(id+"F2.wireOp",EDGE,"E9");var subQ1=sQuery(id+"F2.wireOp",EDGE,"E8");Q83=makeQuery(id+"F13.boolean.opBoolean","SPLIT",EDGE,{"disambiguationData":[TD([makeQuery(id+"F3.boolean.opBoolean","COPY",FACE,{"derivedFrom":makeQuery(id+"F3.opExtrude","SWEPT_FACE",FACE,{"disambiguationData":[OSD([subQ0])]})})])],"derivedFrom":makeQuery(id+"F3.boolean.opBoolean","COPY",EDGE,{"derivedFrom":makeQuery(id+"F3.opExtrude","CAP_EDGE",EDGE,{"disambiguationData":[OSD([subQ1])],"isStart":false})})});}
            var Q84;
            Q84=makeQuery(id+"F15.boolean.opBoolean","COPY",EDGE,{"derivedFrom":makeQuery(id+"F15.opExtrude","CAP_EDGE",EDGE,{"disambiguationData":[OSD([sQuery(id+"F14.wireOp",EDGE,"E77")])],"isStart":false})});
            var Q85;
            {var subQ0=sQuery(id+"F2.wireOp",EDGE,"E12.MirrorCS");var subQ1=sQuery(id+"F2.wireOp",EDGE,"E11.MirrorCS");Q85=makeQuery(id+"F13.boolean.opBoolean","SPLIT",EDGE,{"disambiguationData":[TD([makeQuery(id+"F3.boolean.opBoolean","COPY",FACE,{"derivedFrom":makeQuery(id+"F3.opExtrude","SWEPT_FACE",FACE,{"disambiguationData":[OSD([subQ1])]})})])],"derivedFrom":makeQuery(id+"F3.boolean.opBoolean","COPY",EDGE,{"derivedFrom":makeQuery(id+"F3.opExtrude","CAP_EDGE",EDGE,{"disambiguationData":[OSD([subQ0])],"isStart":false})})});}
            var Q86;
            Q86=makeQuery(id+"F15.boolean.opBoolean","COPY",EDGE,{"derivedFrom":makeQuery(id+"F15.opExtrude","CAP_EDGE",EDGE,{"disambiguationData":[OSD([sQuery(id+"F14.wireOp",EDGE,"E79.MirrorCS")])],"isStart":false})});
            var Q87;
            Q87=makeQuery(id+"F11.boolean.opBoolean","INTERSECT",EDGE,{"derivedFrom":[makeQuery(id+"F3.boolean.opBoolean","COPY",FACE,{"derivedFrom":makeQuery(id+"F3.opExtrude","CAP_FACE",FACE,{"disambiguationData":[OSD([sQuery(id+"F2.wireOp",EDGE,"E11.MirrorCS"),sQuery(id+"F2.wireOp",EDGE,"E12.MirrorCS"),sQuery(id+"F2.wireOp",EDGE,"E13.MirrorCS"),sQuery(id+"F2.wireOp",EDGE,"E14.MirrorCS")])],"isStart":false})}),makeQuery(id+"F11.opExtrude","SWEPT_FACE",FACE,{"disambiguationData":[OSD([sQuery(id+"F10.wireOp",EDGE,"E66.MirrorCS")])]})]});
            var Q88;
            Q88=makeQuery(id+"F3.boolean.opBoolean","COPY",EDGE,{"derivedFrom":makeQuery(id+"F3.opExtrude","CAP_EDGE",EDGE,{"disambiguationData":[OSD([sQuery(id+"F2.wireOp",EDGE,"E14.MirrorCS")])],"isStart":false})});
            var Q89;
            Q89=makeQuery(id+"F3.boolean.opBoolean","COPY",EDGE,{"derivedFrom":makeQuery(id+"F3.opExtrude","CAP_EDGE",EDGE,{"disambiguationData":[OSD([sQuery(id+"F2.wireOp",EDGE,"E10")])],"isStart":false})});
            var Q90;
            Q90=makeQuery(id+"F11.boolean.opBoolean","INTERSECT",EDGE,{"derivedFrom":[makeQuery(id+"F3.boolean.opBoolean","COPY",FACE,{"derivedFrom":makeQuery(id+"F3.opExtrude","CAP_FACE",FACE,{"disambiguationData":[OSD([sQuery(id+"F2.wireOp",EDGE,"E7"),sQuery(id+"F2.wireOp",EDGE,"E8"),sQuery(id+"F2.wireOp",EDGE,"E9"),sQuery(id+"F2.wireOp",EDGE,"E10")])],"isStart":false})}),makeQuery(id+"F11.opExtrude","SWEPT_FACE",FACE,{"disambiguationData":[OSD([sQuery(id+"F10.wireOp",EDGE,"E63")])]})]});
            var Q91;
            Q91=makeQuery(id+"F13.boolean.opBoolean","MERGE",EDGE,{"derivedFrom":[makeQuery(id+"F5.boolean.opBoolean","COPY",EDGE,{"derivedFrom":makeQuery(id+"F5.opExtrude","CAP_EDGE",EDGE,{"disambiguationData":[OSD([sQuery(id+"F4.wireOp",EDGE,"E21.MirrorCS")])],"isStart":false})}),makeQuery(id+"F13.opExtrude","CAP_EDGE",EDGE,{"disambiguationData":[OSD([sQuery(id+"F12.wireOp",EDGE,"E72.MirrorCS")])],"isStart":true})]});
            var Q92;
            Q92=makeQuery(id+"F13.boolean.opBoolean","MERGE",EDGE,{"derivedFrom":[makeQuery(id+"F5.boolean.opBoolean","COPY",EDGE,{"derivedFrom":makeQuery(id+"F5.opExtrude","CAP_EDGE",EDGE,{"disambiguationData":[OSD([sQuery(id+"F4.wireOp",EDGE,"E18")])],"isStart":false})}),makeQuery(id+"F13.opExtrude","CAP_EDGE",EDGE,{"disambiguationData":[OSD([sQuery(id+"F12.wireOp",EDGE,"E70")])],"isStart":true})]});
            chamfer(context, id + "F18", {"entities" : qUnion([Q0, Q1, Q2, Q3, Q4, Q5, Q6, Q7, Q8, Q9, Q10, Q11, Q12, Q13, Q14, Q15, Q16, Q17, Q18, Q19, Q20, Q21, Q22, Q23, Q24, Q25, Q26, Q27, Q28, Q29, Q30, Q31, Q32, Q33, Q34, Q35, Q36, Q37, Q38, Q39, Q40, Q41, Q42, Q43, Q44, Q45, Q46, Q47, Q48, Q49, Q50, Q51, Q52, Q53, Q54, Q55, Q56, Q57, Q58, Q59, Q60, Q61, Q62, Q63, Q64, Q65, Q66, Q67, Q68, Q69, Q70, Q71, Q72, Q73, Q74, Q75, Q76, Q77, Q78, Q79, Q80, Q81, Q82, Q83, Q84, Q85, Q86, Q87, Q88, Q89, Q90, Q91, Q92]), "width" : 0.8 * mm, "tangentPropagation" : true});
        }
        {
            var Q0;
            Q0=makeQuery(id+"F13.boolean.opBoolean","MERGE",EDGE,{"derivedFrom":[makeQuery(id+"F1.opExtrude","CAP_EDGE",EDGE,{"disambiguationData":[OSD([sQuery(id+"F0.wireOp",EDGE,"E3")])],"isStart":true}),makeQuery(id+"F13.opExtrude","CAP_EDGE",EDGE,{"disambiguationData":[OSD([sQuery(id+"F12.wireOp",EDGE,"E70")])],"isStart":false})]});
            var Q1;
            Q1=makeQuery(id+"F13.boolean.opBoolean","MERGE",EDGE,{"derivedFrom":[makeQuery(id+"F1.opExtrude","CAP_EDGE",EDGE,{"disambiguationData":[OSD([sQuery(id+"F0.wireOp",EDGE,"E5.MirrorCS")])],"isStart":true}),makeQuery(id+"F13.opExtrude","CAP_EDGE",EDGE,{"disambiguationData":[OSD([sQuery(id+"F12.wireOp",EDGE,"E72.MirrorCS")])],"isStart":false})]});
            chamfer(context, id + "F19", {"entities" : qUnion([Q0, Q1]), "width" : 3.17 * mm, "tangentPropagation" : true});
        }
    });
